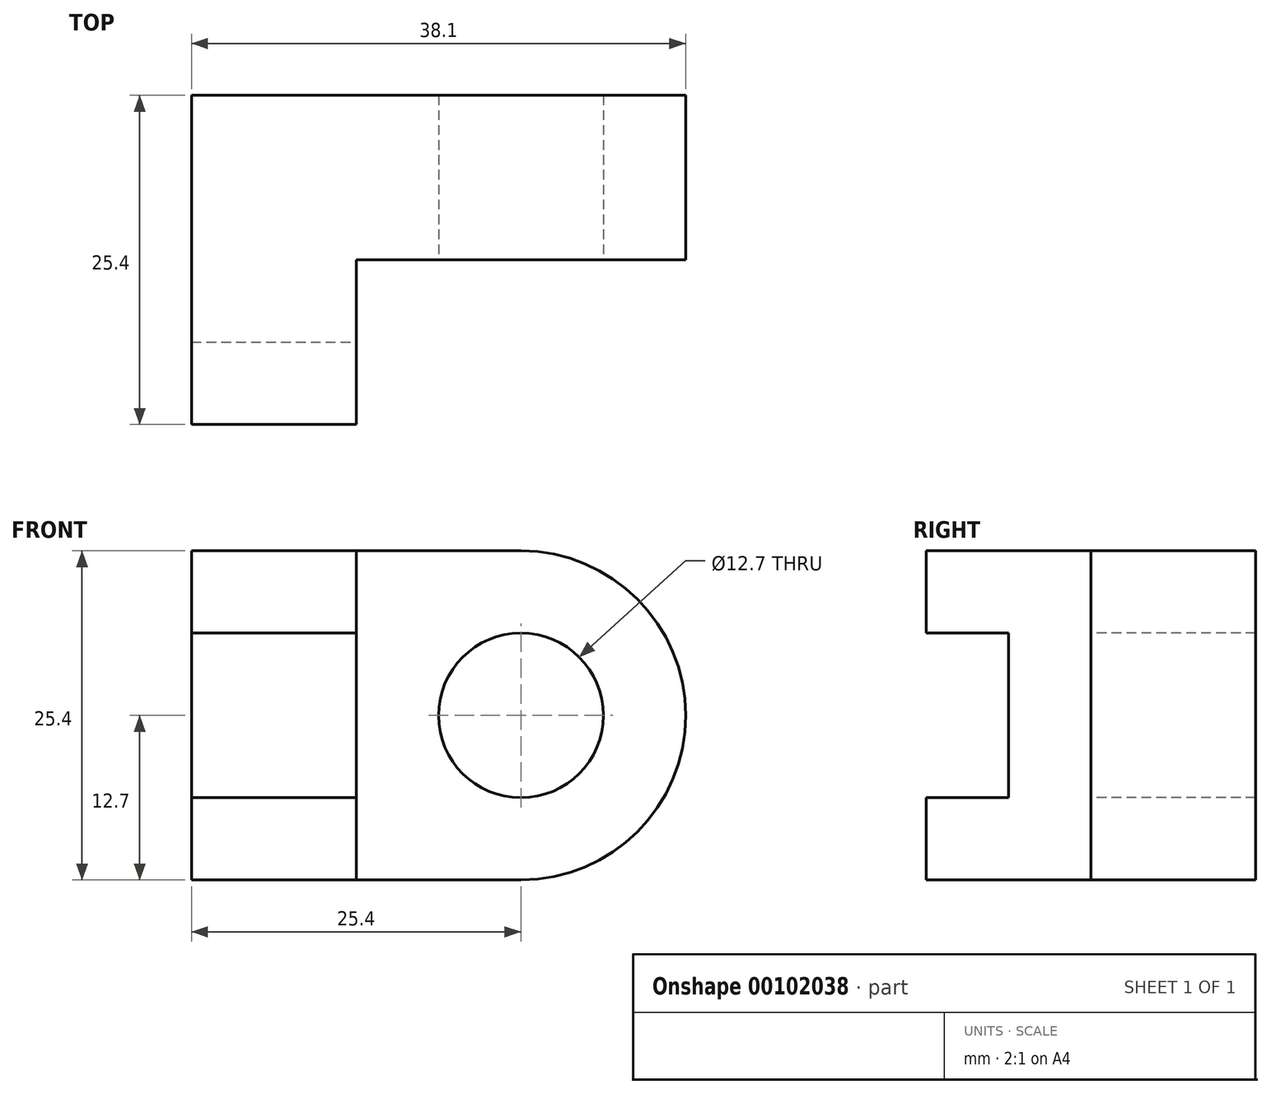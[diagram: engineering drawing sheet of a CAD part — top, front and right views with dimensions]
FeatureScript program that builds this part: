
annotation { "Feature Type Name" : "Feature", "Feature Type Description" : "" }
export const myFeature = defineFeature(function(context is Context, id is Id, definition is map)
    precondition{}
    {
        {
            var Q0;
            Q0=qCreatedBy(makeId("Front.planeOp"),FACE);
            var sketch = newSketch(context, id + "F0", { "sketchPlane" : qUnion([Q0])});
            skLineSegment(sketch, "E0", {"start": v(25.4, 0) * mm, "end": v(0, 0) * mm});
            skLineSegment(sketch, "E1", {"start": v(0, 0) * mm, "end": v(0, 25.4) * mm});
            skLineSegment(sketch, "E2", {"start": v(0, 25.4) * mm, "end": v(25.4, 25.4) * mm});
            skArc(sketch, "E3", {"start": v(25.4, 0) * mm, "mid": v(38.1, 12.7) * mm, "end": v(25.4, 25.4) * mm});
            skSolve(sketch);
        }
        {
            var Q0;
            Q0=makeQuery(id+"F0.imprint","IMPRINT",FACE,{"disambiguationData":[TD([[makeQuery(id+"F0.imprint","IMPRINT",EDGE,{"derivedFrom":sQuery(id+"F0.wireOp",EDGE,"E0")}),-1.0]])]});
            extrude(context, id + "F1", {"entities" : qUnion([Q0]), "depth" : 12.7 * mm});
        }
        {
            var Q0;
            Q0=makeQuery(id+"F1.opExtrude","CAP_FACE",FACE,{"disambiguationData":[OSD([sQuery(id+"F0.wireOp",EDGE,"E0"),sQuery(id+"F0.wireOp",EDGE,"E1"),sQuery(id+"F0.wireOp",EDGE,"E2"),sQuery(id+"F0.wireOp",EDGE,"E3")])],"isStart":false});
            var sketch = newSketch(context, id + "F2", { "sketchPlane" : qUnion([Q0])});
            skCircle(sketch, "E4", {"center": v(25.4, 12.7) * mm, "radius": 6.35 * mm});
            skSolve(sketch);
        }
        {
            var Q0;
            Q0=makeQuery(id+"F2.imprint","IMPRINT",FACE,{"disambiguationData":[TD([[makeQuery(id+"F2.imprint","IMPRINT",EDGE,{"derivedFrom":sQuery(id+"F2.wireOp",EDGE,"E4")}),1.0]])]});
            extrude(context, id + "F3", {"entities" : qUnion([Q0]), "operationType" : NewBodyOperationType.REMOVE, "endBound" : BoundingType.THROUGH_ALL, "oppositeDirection" : true, "depth" : 25.4 * mm});
        }
        {
            var Q0;
            Q0=makeQuery(id+"F1.opExtrude","CAP_FACE",FACE,{"disambiguationData":[OSD([sQuery(id+"F0.wireOp",EDGE,"E0"),sQuery(id+"F0.wireOp",EDGE,"E1"),sQuery(id+"F0.wireOp",EDGE,"E2"),sQuery(id+"F0.wireOp",EDGE,"E3")])],"isStart":false});
            var sketch = newSketch(context, id + "F4", { "sketchPlane" : qUnion([Q0])});
            skLineSegment(sketch, "E5.bottom", {"start": v(0, 25.4) * mm, "end": v(12.7, 25.4) * mm});
            skLineSegment(sketch, "E5.top", {"start": v(0, 0) * mm, "end": v(12.7, 0) * mm});
            skLineSegment(sketch, "E5.left", {"start": v(0, 25.4) * mm, "end": v(0, 0) * mm});
            skLineSegment(sketch, "E5.right", {"start": v(12.7, 25.4) * mm, "end": v(12.7, 0) * mm});
            skSolve(sketch);
        }
        {
            var Q0;
            Q0 = qSketchRegion(id + "F4", true);
            extrude(context, id + "F5", {"entities" : qUnion([Q0]), "operationType" : NewBodyOperationType.ADD, "depth" : 12.7 * mm});
        }
        {
            var Q0;
            Q0=makeQuery(id+"F5.opExtrude","SWEPT_FACE",FACE,{"disambiguationData":[OSD([sQuery(id+"F4.wireOp",EDGE,"E5.right")])]});
            var sketch = newSketch(context, id + "F6", { "sketchPlane" : qUnion([Q0])});
            skLineSegment(sketch, "E6.bottom", {"start": v(-25.4, 19.05) * mm, "end": v(-19.05, 19.05) * mm});
            skLineSegment(sketch, "E6.top", {"start": v(-25.4, 6.35) * mm, "end": v(-19.05, 6.35) * mm});
            skLineSegment(sketch, "E6.left", {"start": v(-25.4, 19.05) * mm, "end": v(-25.4, 6.35) * mm});
            skLineSegment(sketch, "E6.right", {"start": v(-19.05, 19.05) * mm, "end": v(-19.05, 6.35) * mm});
            skSolve(sketch);
        }
        {
            var Q0;
            Q0=makeQuery(id+"F6.imprint","IMPRINT",FACE,{"disambiguationData":[TD([[makeQuery(id+"F6.imprint","IMPRINT",EDGE,{"derivedFrom":sQuery(id+"F6.wireOp",EDGE,"E6.bottom")}),-1.0]])]});
            extrude(context, id + "F7", {"entities" : qUnion([Q0]), "operationType" : NewBodyOperationType.REMOVE, "endBound" : BoundingType.THROUGH_ALL, "oppositeDirection" : true, "depth" : 25.4 * mm});
        }
    });
